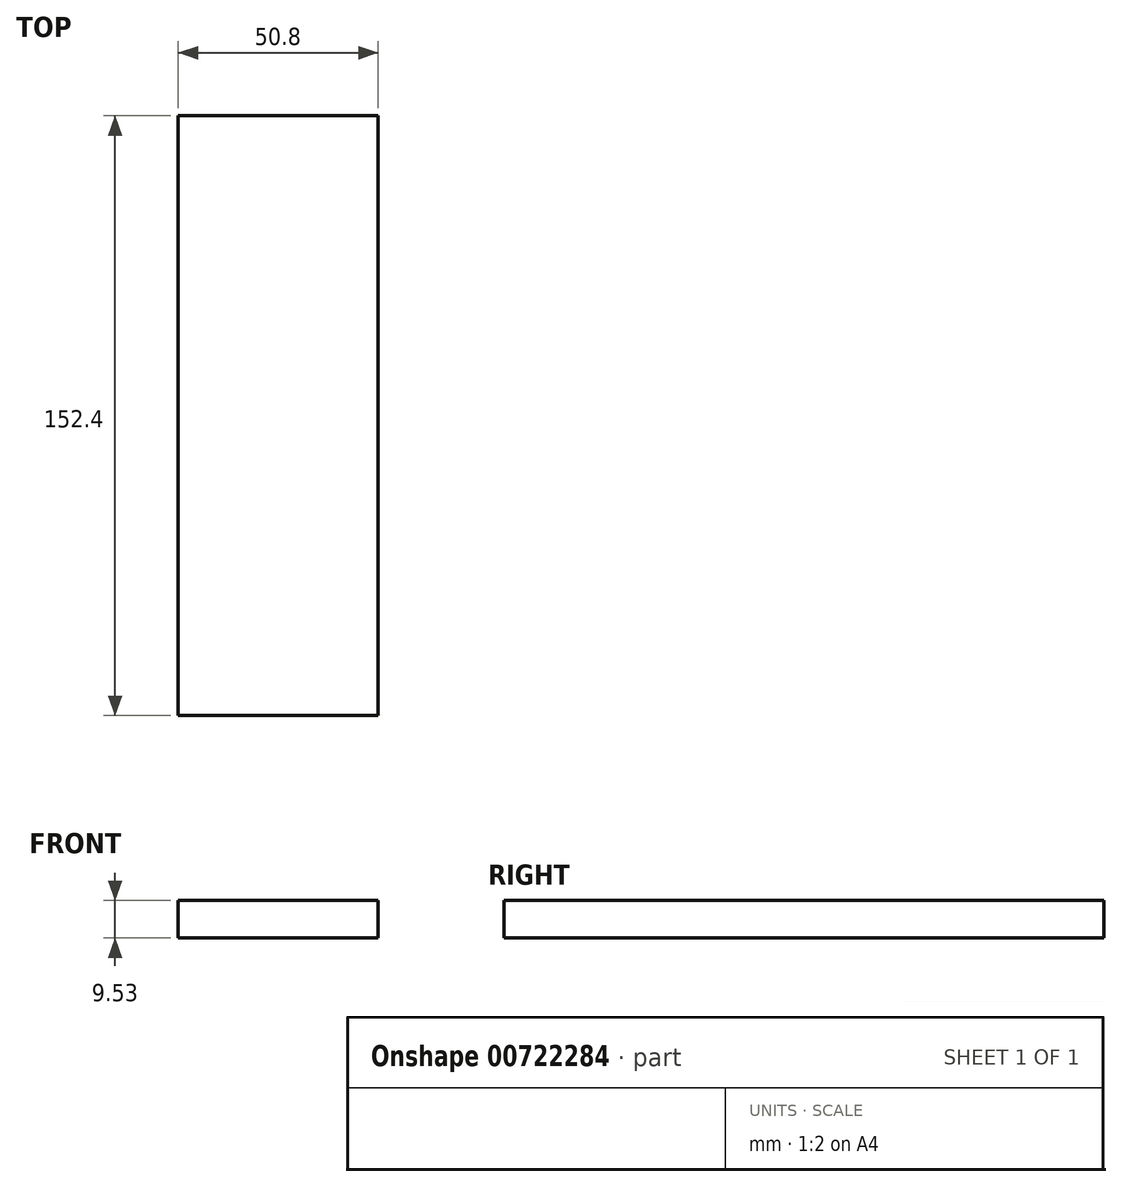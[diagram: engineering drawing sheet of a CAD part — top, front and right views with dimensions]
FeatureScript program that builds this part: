
annotation { "Feature Type Name" : "Feature", "Feature Type Description" : "" }
export const myFeature = defineFeature(function(context is Context, id is Id, definition is map)
    precondition{}
    {
        {
            var Q0;
            Q0=qCreatedBy(makeId("Top.planeOp"),FACE);
            var sketch = newSketch(context, id + "F0", { "sketchPlane" : qUnion([Q0])});
            skLineSegment(sketch, "E0.bottom", {"start": v(0, 0) * mm, "end": v(50.8, 0) * mm});
            skLineSegment(sketch, "E0.top", {"start": v(0, -152.4) * mm, "end": v(50.8, -152.4) * mm});
            skLineSegment(sketch, "E0.left", {"start": v(0, 0) * mm, "end": v(0, -152.4) * mm});
            skLineSegment(sketch, "E0.right", {"start": v(50.8, 0) * mm, "end": v(50.8, -152.4) * mm});
            skSolve(sketch);
        }
        {
            var Q0;
            Q0=makeQuery(id+"F0.imprint","IMPRINT",FACE,{"disambiguationData":[TD([[makeQuery(id+"F0.imprint","IMPRINT",EDGE,{"derivedFrom":sQuery(id+"F0.wireOp",EDGE,"E0.bottom")}),-1.0]])]});
            extrude(context, id + "F1", {"entities" : qUnion([Q0]), "depth" : 9.52 * mm, "offsetDistance" : 25.4 * mm});
        }
    });
